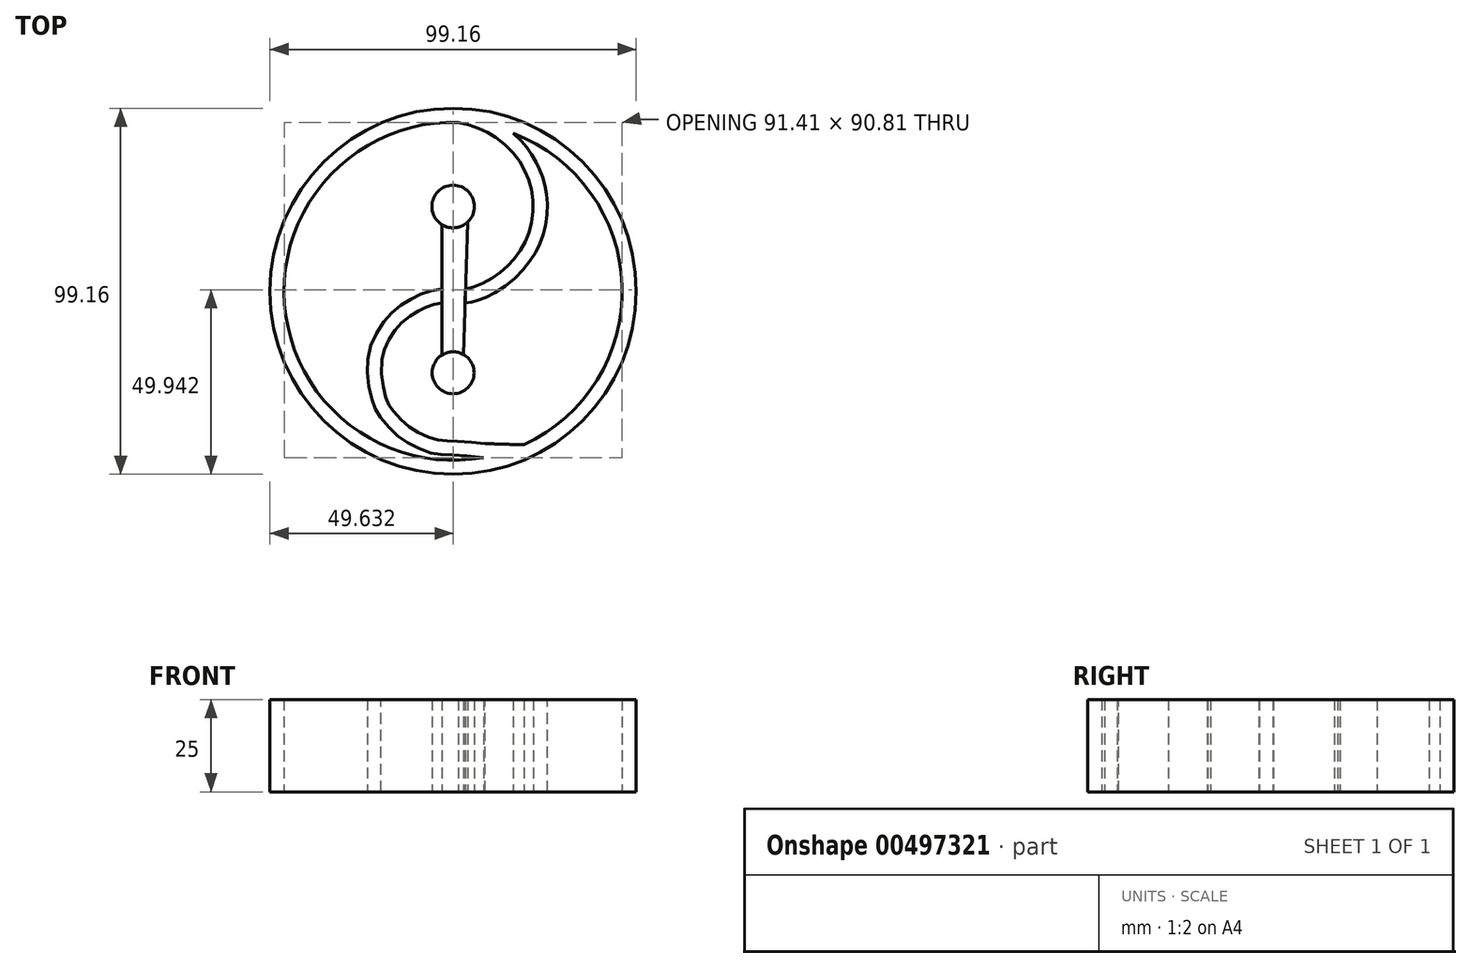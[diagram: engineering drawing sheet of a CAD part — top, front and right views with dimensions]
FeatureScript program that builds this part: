
annotation { "Feature Type Name" : "Feature", "Feature Type Description" : "" }
export const myFeature = defineFeature(function(context is Context, id is Id, definition is map)
    precondition{}
    {
        {
            var Q0;
            Q0=qCreatedBy(makeId("Top.planeOp"),FACE);
            var sketch = newSketch(context, id + "F0", { "sketchPlane" : qUnion([Q0])});
            skArc(sketch, "E0", {"start": v(1.35, 45.76) * mm, "mid": v(-45.65, -3.45) * mm, "end": v(8.22, -45.04) * mm});
            skFitSpline(sketch, "E1", {"points": [v(1.35, 45.76) * mm, v(7.24, 43.98) * mm, v(11.59, 41.63) * mm, v(16.84, 36.8) * mm, v(19.74, 31.82) * mm, v(21.47, 26.5) * mm, v(21.47, 19.87) * mm, v(20.02, 14.34) * mm, v(17.05, 9.5) * mm, v(13.6, 5.84) * mm, v(9.1, 2.73) * mm, v(4.34, 0.8) * mm, v(1.5, 0.58) * mm, v(-1.67, 0.65) * mm, v(-6.57, 0) * mm, v(-10.93, -1.9) * mm, v(-15.58, -4.87) * mm, v(-19.36, -9) * mm, v(-22.67, -16.03) * mm, v(-23.13, -23.23) * mm, v(-21.74, -30.26) * mm, v(-20.1, -33.52) * mm, v(-15.93, -38.4) * mm, v(-11.22, -41.65) * mm, v(-5.47, -43.92) * mm, v(-1.23, -44.32) * mm, v(8.22, -45.04) * mm], "startDerivative": vector(156.8, -26.62) * mm, "endDerivative": vector(210.3, -21.2) * mm});
            skCircle(sketch, "E2", {"center": v(0, 22.95) * mm, "radius": 5.76 * mm});
            skCircle(sketch, "E3", {"center": v(0, -22.09) * mm, "radius": 5.68 * mm});
            skCircle(sketch, "E4.0", {"center": v(0, 0) * mm, "radius": 49.58 * mm});
            skFitSpline(sketch, "E5.0", {"points": [v(1.99, 49.51) * mm, v(2.96, 49.35) * mm, v(4.37, 49.01) * mm, v(6.13, 48.47) * mm, v(7.37, 48.02) * mm, v(8.34, 47.64) * mm, v(9.07, 47.33) * mm, v(9.8, 47.01) * mm, v(10.71, 46.58) * mm, v(12.17, 45.81) * mm, v(14, 44.64) * mm, v(15.9, 43.14) * mm, v(17.39, 41.8) * mm, v(18.47, 40.72) * mm, v(19.32, 39.77) * mm, v(19.96, 38.98) * mm, v(20.56, 38.18) * mm, v(21.23, 37.19) * mm, v(21.93, 36) * mm, v(22.53, 34.85) * mm, v(22.97, 33.92) * mm, v(23.3, 33.2) * mm, v(23.62, 32.45) * mm, v(24.01, 31.48) * mm, v(24.46, 30.23) * mm, v(24.85, 28.9) * mm, v(25.12, 27.73) * mm, v(25.28, 26.75) * mm, v(25.4, 25.76) * mm, v(25.5, 24.53) * mm, v(25.52, 22.58) * mm, v(25.4, 20.66) * mm, v(25.18, 18.85) * mm, v(24.95, 17.51) * mm, v(24.66, 16.18) * mm, v(24.29, 14.86) * mm, v(23.83, 13.56) * mm, v(23.27, 12.27) * mm, v(22.64, 11.04) * mm, v(21.72, 9.47) * mm, v(20.72, 8.03) * mm, v(19.7, 6.7) * mm, v(18.63, 5.44) * mm, v(17.22, 3.95) * mm, v(15.35, 2.3) * mm, v(13.28, 0.78) * mm, v(11.41, -0.36) * mm, v(9.83, -1.2) * mm, v(8.62, -1.76) * mm, v(7.6, -2.17) * mm, v(6.77, -2.47) * mm, v(6.15, -2.66) * mm, v(5.53, -2.84) * mm, v(4.9, -2.98) * mm, v(4.28, -3.09) * mm, v(3.49, -3.19) * mm, v(2.57, -3.24) * mm, v(1.77, -3.23) * mm, v(1.2, -3.2) * mm, v(0.66, -3.19) * mm, v(0, -3.16) * mm, v(-0.78, -3.14) * mm, v(-1.57, -3.14) * mm, v(-2.44, -3.18) * mm, v(-3.34, -3.25) * mm, v(-4.1, -3.35) * mm, v(-4.67, -3.45) * mm, v(-5.08, -3.54) * mm, v(-5.47, -3.64) * mm, v(-5.96, -3.78) * mm, v(-6.56, -3.99) * mm, v(-7.3, -4.3) * mm, v(-7.96, -4.63) * mm, v(-8.52, -4.92) * mm, v(-8.96, -5.16) * mm, v(-9.42, -5.41) * mm, v(-10.02, -5.75) * mm, v(-10.77, -6.19) * mm, v(-11.64, -6.72) * mm, v(-12.46, -7.27) * mm, v(-13.2, -7.82) * mm, v(-13.87, -8.38) * mm, v(-14.48, -8.97) * mm, v(-15.07, -9.6) * mm, v(-15.65, -10.32) * mm, v(-16.23, -11.14) * mm, v(-16.82, -12.07) * mm, v(-17.4, -13.07) * mm, v(-17.92, -14.12) * mm, v(-18.4, -15.2) * mm, v(-18.72, -16.07) * mm, v(-18.93, -16.76) * mm, v(-19.1, -17.42) * mm, v(-19.35, -18.57) * mm, v(-19.5, -20.22) * mm, v(-19.44, -22.03) * mm, v(-19.27, -23.64) * mm, v(-19.1, -24.88) * mm, v(-18.87, -26.1) * mm, v(-18.63, -27.27) * mm, v(-18.36, -28.32) * mm, v(-18.1, -29.2) * mm, v(-17.86, -29.82) * mm, v(-17.64, -30.3) * mm, v(-17.41, -30.7) * mm, v(-17.16, -31.1) * mm, v(-16.93, -31.44) * mm, v(-16.66, -31.81) * mm, v(-16.27, -32.34) * mm, v(-15.71, -33.05) * mm, v(-14.98, -33.92) * mm, v(-14.2, -34.77) * mm, v(-13.44, -35.53) * mm, v(-12.73, -36.17) * mm, v(-12.01, -36.73) * mm, v(-11.28, -37.24) * mm, v(-10.5, -37.73) * mm, v(-9.61, -38.21) * mm, v(-8.64, -38.7) * mm, v(-7.62, -39.17) * mm, v(-6.61, -39.58) * mm, v(-5.65, -39.93) * mm, v(-4.8, -40.18) * mm, v(-4.13, -40.32) * mm, v(-3.48, -40.4) * mm, v(-2.73, -40.46) * mm, v(-1.94, -40.5) * mm, v(-1.2, -40.52) * mm, v(-0.38, -40.56) * mm, v(0.72, -40.62) * mm, v(2.15, -40.7) * mm, v(3.68, -40.82) * mm, v(5.81, -41) * mm, v(7.48, -41.15) * mm, v(8.6, -41.26) * mm]});
            skFitSpline(sketch, "E6", {"points": [v(8.6, -41.26) * mm, v(19.14, -41.6) * mm], "startDerivative": vector(10.57, -0.31) * mm, "endDerivative": vector(10.57, -0.31) * mm});
            skArc(sketch, "E7.trimOffspring", {"start": v(19.14, -41.6) * mm, "mid": v(45.76, 1.56) * mm, "end": v(16.26, 42.8) * mm});
            skLineSegment(sketch, "E8", {"start": v(-2.98, 18) * mm, "end": v(-2.98, -17.25) * mm});
            skLineSegment(sketch, "E9", {"start": v(3.9, 18.7) * mm, "end": v(2.78, -17.13) * mm});
            skSolve(sketch);
        }
        {
            var Q0;
            Q0=makeQuery(id+"F0.imprint","IMPRINT",FACE,{"disambiguationData":[TD([[makeQuery(id+"F0.imprint","IMPRINT",EDGE,{"derivedFrom":sQuery(id+"F0.wireOp",EDGE,"E4.0")}),1.0]])]});
            var Q1;
            {var subQ4=sQuery(id+"F0.wireOp",EDGE,"E1");Q1=makeQuery(id+"F0.imprint","IMPRINT",FACE,{"disambiguationData":[TD([[makeQuery(id+"F0.imprint","IMPRINT",EDGE,{"derivedFrom":subQ4}),1.0]])]});}
            extrude(context, id + "F1", {"entities" : qUnion([Q0, Q1]), "depth" : 25 * mm});
        }
        {
            var Q0;
            Q0=makeQuery(id+"F0.imprint","IMPRINT",FACE,{"disambiguationData":[TD([[makeQuery(id+"F0.imprint","IMPRINT",EDGE,{"derivedFrom":sQuery(id+"F0.wireOp",EDGE,"E2")}),1.0]])]});
            var Q1;
            Q1=makeQuery(id+"F0.imprint","IMPRINT",FACE,{"disambiguationData":[TD([[makeQuery(id+"F0.imprint","IMPRINT",EDGE,{"derivedFrom":sQuery(id+"F0.wireOp",EDGE,"E3")}),1.0]])]});
            extrude(context, id + "F2", {"entities" : qUnion([Q0, Q1]), "depth" : 25 * mm});
        }
        {
            var Q0;
            {var subQ0=sQuery(id+"F0.wireOp",EDGE,"E9");var subQ1=sQuery(id+"F0.wireOp",EDGE,"E1");var subQ2=makeQuery(id+"F0.imprint","INTERSECT",VERTEX,{"derivedFrom":[subQ1,subQ0]});Q0=makeQuery(id+"F0.imprint","IMPRINT",FACE,{"disambiguationData":[TD([[makeQuery(id+"F0.imprint","IMPRINT",EDGE,{"disambiguationData":[TD([[subQ2,-1.0]])],"derivedFrom":subQ1}),-1.0]])]});}
            var Q1;
            {var subQ0=sQuery(id+"F0.wireOp",EDGE,"E8");var subQ1=sQuery(id+"F0.wireOp",EDGE,"E3");var subQ2=makeQuery(id+"F0.imprint","INTERSECT",VERTEX,{"derivedFrom":[subQ1,subQ0]});Q1=makeQuery(id+"F0.imprint","IMPRINT",FACE,{"disambiguationData":[TD([[makeQuery(id+"F0.imprint","IMPRINT",EDGE,{"disambiguationData":[TD([[subQ2,1.0]])],"derivedFrom":subQ1}),-1.0]])]});}
            var Q2;
            {var subQ0=sQuery(id+"F0.wireOp",EDGE,"E9");var subQ1=sQuery(id+"F0.wireOp",EDGE,"E1");var subQ2=makeQuery(id+"F0.imprint","INTERSECT",VERTEX,{"derivedFrom":[subQ1,subQ0]});Q2=makeQuery(id+"F0.imprint","IMPRINT",FACE,{"disambiguationData":[TD([[makeQuery(id+"F0.imprint","IMPRINT",EDGE,{"disambiguationData":[TD([[subQ2,-1.0]])],"derivedFrom":subQ1}),1.0]])]});}
            extrude(context, id + "F3", {"entities" : qUnion([Q0, Q1, Q2]), "depth" : 25 * mm});
        }
    });
